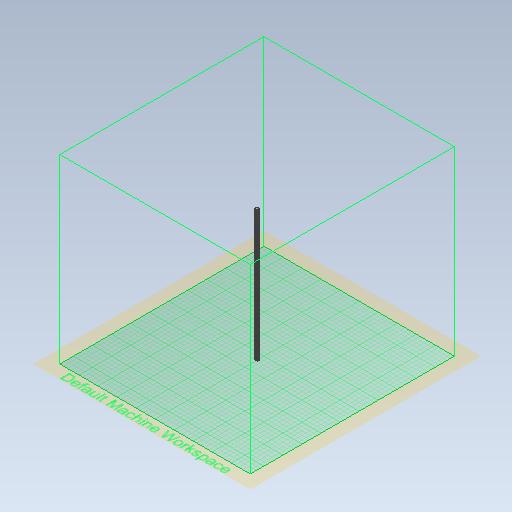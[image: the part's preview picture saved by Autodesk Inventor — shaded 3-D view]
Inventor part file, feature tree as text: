
AUTODESK INVENTOR PART (.ipt)
format: ipt  version: 2020 (Build 240168000, 168)  size: 1,341,440 bytes
history: native  units: mm
features: sketch x2, extrude x1, chamfer x1, other x1
ambient origin geometry x8: Origin, YZ Plane, XZ Plane, XY Plane, X Axis, Y Axis, Z Axis, Center Point
bodies: Solid1 (feature_tree)
feature tree (5):
  extrude  "D8 Rod (400mm)"  Depth=400.0mm TaperAngle=0.0deg
  chamfer  "Chamfer1"  Distance=5.061455mm
  other  "P2 ACME Thread"
  sketch  "Sketch1"  dims[d0=8.0mm d1=400.0mm d2=0.0mm]
  sketch  "Sketch2"  dims[d8=2.0mm d9=522.0mm d10=10.0mm d11=0.0mm d12=90.0deg d13=90.0deg d14=0.0mm d15=0.0mm d17=5.061455mm d18=1.0mm d19=0.7414mm d20=1.0mm d21=2.0mm d22=45.0deg d23=0.5mm d24=0.872665mm d25=0.5mm d26=0.872665mm]
